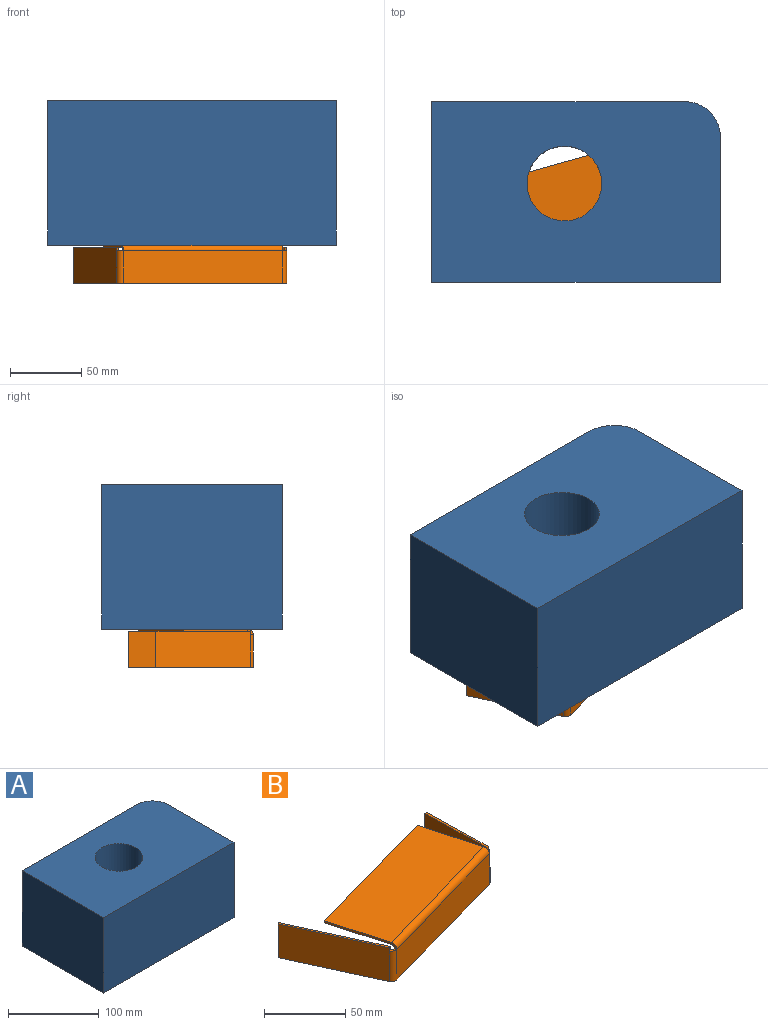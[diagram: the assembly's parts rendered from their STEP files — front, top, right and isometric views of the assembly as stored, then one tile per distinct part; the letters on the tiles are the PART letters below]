
ASSEMBLY  parts=2 mates=1
PART A: 8 faces, bbox 203.2x127x101.6 mm
  f0: plane 177.8x101.6mm, normal (0,1,0), area 18064.5mm2, adj f1,f5,f6,f7
  f1: plane 127x101.6mm, normal (-1,0,0), area 12903.2mm2, adj f0,f2,f6,f7
  f2: plane 203.2x101.6mm, normal (0,-1,0), area 20645.1mm2, adj f1,f3,f6,f7
  f3: plane 101.6x101.6mm, normal (1,0,0), area 10322.6mm2, adj f2,f5,f6,f7
  f4: cylinder r=26.3mm len=101.6mm, axis (0,0,-1), area 16789.2mm2, adj f6,f7
  f5: cylinder r=25.4mm len=101.6mm, axis (0,0,-1), area 4053.7mm2, adj f0,f3,f6,f7
  f6: plane 203.2x127mm, normal (0,0,1), area 23494.9mm2, adj f0,f1,f2,f3,f4,f5
  f7: plane 203.2x127mm, normal (0,0,-1), area 23494.9mm2, adj f0,f1,f2,f3,f4,f5
PART B: 32 faces, bbox 149.7x88.2x27 mm
  f0: plane 66.94x31.72mm, normal (0,0,-1), area 115.7mm2, adj f3,f4,f5,f29
  f1: plane 2.29x1.44mm, normal (0.42,-0.91,0), area 3.6mm2, adj f2,f4,f5,f28
  f2: plane 66.94x31.72mm, normal (0,0,1), area 115.7mm2, adj f1,f3,f4,f5
  f3: plane 25.4x1.44mm, normal (-0.42,0.91,0), area 40.3mm2, adj f0,f2,f4,f5
  f4: plane 66.28x30.28mm, normal (-0.91,-0.42,0), area 1850.9mm2, adj f0,f1,f2,f3,f30
  f5: plane 66.28x30.28mm, normal (0.91,0.42,0), area 1850.9mm2, adj f0,f1,f2,f3,f31
  f6: plane 112.5x33.31mm, normal (0,0,-1), area 184.9mm2, adj f7,f8,f16,f29
  f7: plane 112.07x31.78mm, normal (0.27,-0.96,0), area 2692.5mm2, adj f6,f17,f26,f30
  f8: plane 112.07x31.78mm, normal (-0.27,0.96,0), area 2692.5mm2, adj f6,f18,f27,f31
  f9: plane 2.29x1.59mm, normal (0.02,-1,0), area 3.6mm2, adj f12,f13,f14,f15
  f10: plane 52.49x2.69mm, normal (0,0,-1), area 83.3mm2, adj f11,f13,f14,f16
  f11: plane 25.4x1.59mm, normal (-0.02,1,0), area 40.3mm2, adj f10,f12,f13,f14
  f12: plane 52.49x2.69mm, normal (0,0,1), area 83.3mm2, adj f9,f11,f13,f14
  f13: plane 52.46x25.4mm, normal (1,0.02,0), area 1332.8mm2, adj f9,f10,f11,f12,f17
  f14: plane 52.46x25.4mm, normal (-1,-0.02,0), area 1332.8mm2, adj f9,f10,f11,f12,f18
  f15: plane 3.81x3.25mm, normal (0,0,1), area 6.4mm2, adj f9,f17,f18,f25
  f16: plane 3.81x3.25mm, normal (0,0,-1), area 6.4mm2, adj f6,f10,f17,f18
  f17: cylinder r=3.87mm len=23.11mm, axis (0,0,1), area 117.8mm2, adj f7,f13,f15,f16
  f18: cylinder r=2.29mm len=23.11mm, axis (0,0,1), area 69.5mm2, adj f8,f14,f15,f16
  f19: plane 112.07x31.78mm, normal (-0.27,0.96,0), area 184.9mm2, adj f20,f21,f22,f23
  f20: plane 45.15x12.8mm, normal (-0.96,-0.27,0), area 74.5mm2, adj f19,f22,f23,f24
  f21: plane 45.15x12.8mm, normal (0.96,0.27,0), area 74.5mm2, adj f19,f22,f23,f25
  f22: plane 124.87x76.93mm, normal (0,0,1), area 5466.4mm2, adj f19,f20,f21,f26
  f23: plane 124.87x76.93mm, normal (0,0,-1), area 5466.4mm2, adj f19,f20,f21,f27
  f24: plane 3.87x3.73mm, normal (-0.96,-0.27,0), area 7.7mm2, adj f20,f26,f27,f28
  f25: plane 3.87x3.73mm, normal (0.96,0.27,0), area 7.7mm2, adj f15,f21,f26,f27
  f26: cylinder r=3.87mm len=113.12mm, axis (-0.96,-0.27,0), area 708.8mm2, adj f7,f22,f24,f25
  f27: cylinder r=2.29mm len=112.69mm, axis (-0.96,-0.27,0), area 418.3mm2, adj f8,f23,f24,f25
  f28: plane 4.58x2.92mm, normal (0,0,1), area 6.9mm2, adj f1,f24,f30,f31
  f29: plane 4.58x2.92mm, normal (0,0,-1), area 6.9mm2, adj f0,f6,f30,f31
  f30: cylinder r=3.87mm len=23.11mm, axis (0,0,1), area 127mm2, adj f4,f7,f28,f29
  f31: cylinder r=2.29mm len=23.11mm, axis (0,0,1), area 75mm2, adj f5,f8,f28,f29
PLACE A t=(-41.94,-7.24,22.99)mm
PLACE B t=(31.79,73.61,-4)mm
MATE slider A.f7 <-> B.f22  axis (0,0,-1) through (59.84,55.37,22.99)mm
